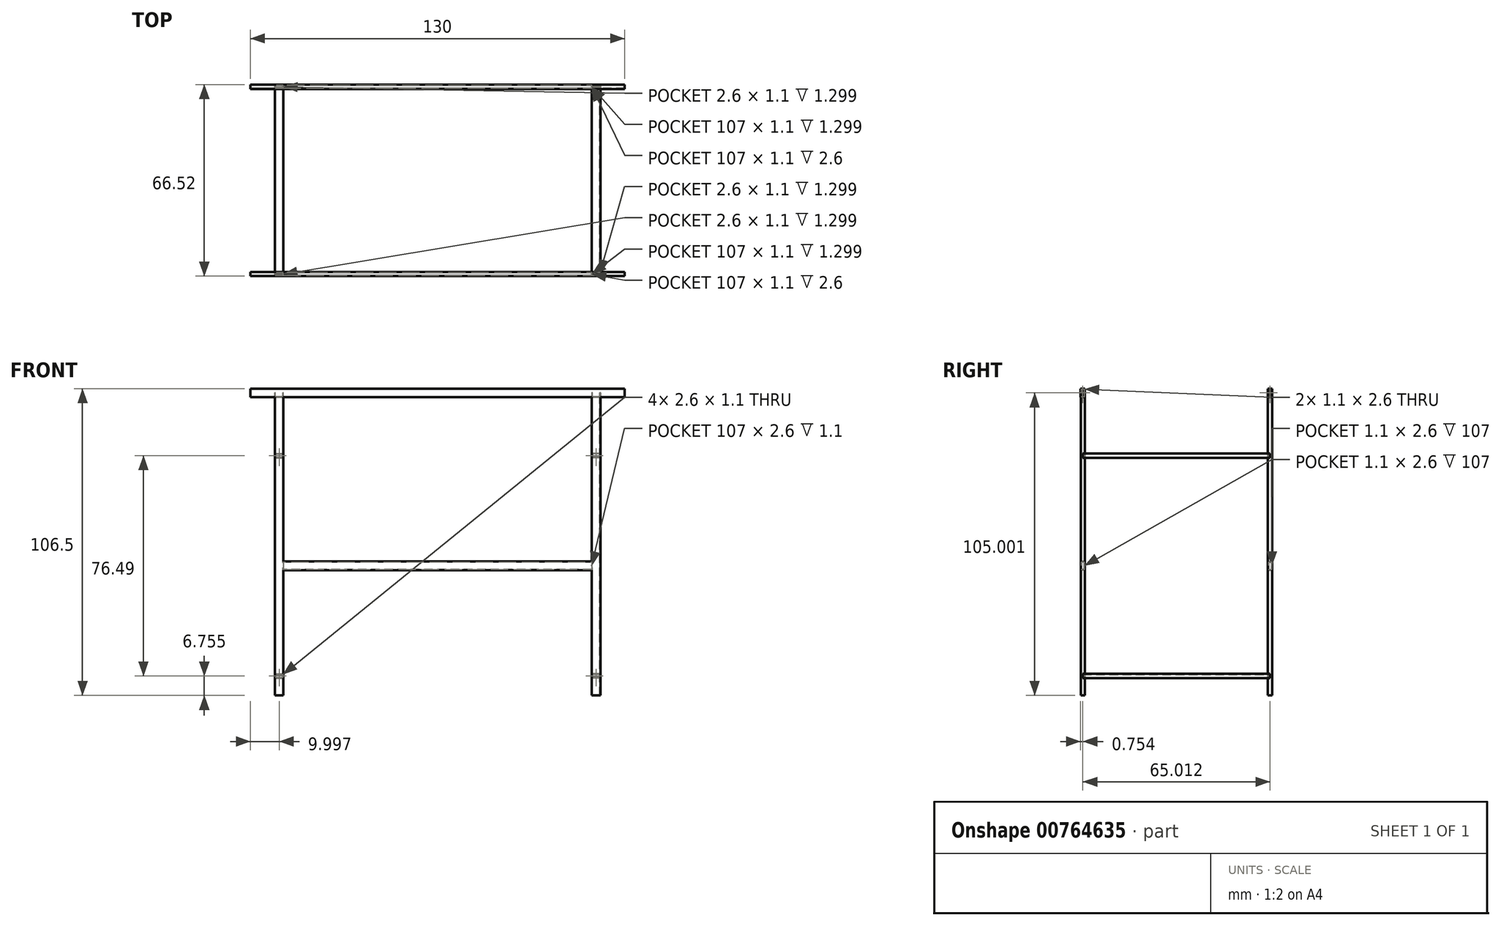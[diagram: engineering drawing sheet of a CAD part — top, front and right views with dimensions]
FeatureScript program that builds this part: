
annotation { "Feature Type Name" : "Feature", "Feature Type Description" : "" }
export const myFeature = defineFeature(function(context is Context, id is Id, definition is map)
    precondition{}
    {
        {
            var Q0;
            Q0=qCreatedBy(makeId("Top.planeOp"),FACE);
            cPlane(context, id + "F0", {"entities" : qUnion([Q0]), "cplaneType" : CPlaneType.OFFSET, "offset" : 60 * mm, "width" : 150 * mm, "height" : 150 * mm});
        }
        {
            var Q0;
            Q0=qCreatedBy(id+"F0.planeOp",FACE);
            var sketch = newSketch(context, id + "F1", { "sketchPlane" : qUnion([Q0])});
            skLineSegment(sketch, "E0", {"start": v(0, 0) * mm, "end": v(-65, 0) * mm, "construction": true});
            skLineSegment(sketch, "E1", {"start": v(-65, 0) * mm, "end": v(-65, 32.5) * mm, "construction": true});
            skSolve(sketch);
        }
        {
            var Q0;
            Q0=qCreatedBy(makeId("Right.planeOp"),FACE);
            cPlane(context, id + "F2", {"entities" : qUnion([Q0]), "cplaneType" : CPlaneType.OFFSET, "offset" : 65 * mm, "oppositeDirection" : true, "width" : 150 * mm, "height" : 150 * mm});
        }
        {
            var Q0;
            Q0=qCreatedBy(id+"F2.planeOp",FACE);
            var sketch = newSketch(context, id + "F3", { "sketchPlane" : qUnion([Q0])});
            skLineSegment(sketch, "E2.bottom", {"start": v(33.26, 61.5) * mm, "end": v(31.76, 61.5) * mm});
            skLineSegment(sketch, "E2.top", {"start": v(33.26, 58.5) * mm, "end": v(31.76, 58.5) * mm});
            skLineSegment(sketch, "E2.left", {"start": v(33.26, 61.5) * mm, "end": v(33.26, 58.5) * mm});
            skLineSegment(sketch, "E2.right", {"start": v(31.76, 61.5) * mm, "end": v(31.76, 58.5) * mm});
            skPoint(sketch, "E2.middle", {"position": v(32.5, 60) * mm});
            skLineSegment(sketch, "E3.bottom", {"start": v(33.06, 61.3) * mm, "end": v(31.96, 61.3) * mm});
            skLineSegment(sketch, "E3.top", {"start": v(33.06, 58.7) * mm, "end": v(31.96, 58.7) * mm});
            skLineSegment(sketch, "E3.left", {"start": v(33.06, 61.3) * mm, "end": v(33.06, 58.7) * mm});
            skLineSegment(sketch, "E3.right", {"start": v(31.96, 61.3) * mm, "end": v(31.96, 58.7) * mm});
            skSolve(sketch);
        }
        {
            var Q0;
            Q0=makeQuery(id+"F3.imprint","IMPRINT",FACE,{"disambiguationData":[TD([[makeQuery(id+"F3.imprint","IMPRINT",EDGE,{"derivedFrom":sQuery(id+"F3.wireOp",EDGE,"E2.bottom")}),1.0]])]});
            extrude(context, id + "F4", {"entities" : qUnion([Q0]), "depth" : 130 * mm, "offsetDistance" : 25 * mm});
        }
        {
            var Q0;
            Q0=makeQuery(id+"F4.opExtrude","SWEPT_BODY",BODY,{"disambiguationData":[OSD([sQuery(id+"F3.wireOp",EDGE,"E2.bottom"),sQuery(id+"F3.wireOp",EDGE,"E2.top"),sQuery(id+"F3.wireOp",EDGE,"E2.left"),sQuery(id+"F3.wireOp",EDGE,"E2.right"),sQuery(id+"F3.wireOp",EDGE,"E3.bottom"),sQuery(id+"F3.wireOp",EDGE,"E3.top"),sQuery(id+"F3.wireOp",EDGE,"E3.left"),sQuery(id+"F3.wireOp",EDGE,"E3.right")])]});
            var Q1;
            Q1=qCreatedBy(makeId("Front.planeOp"),FACE);
            mirror(context, id + "F5", {"entities" : qUnion([Q0]), "mirrorPlane" : qUnion([Q1])});
        }
        {
            var Q0;
            Q0=qCreatedBy(id+"F0.planeOp",FACE);
            var sketch = newSketch(context, id + "F6", { "sketchPlane" : qUnion([Q0])});
            skLineSegment(sketch, "E4", {"start": v(0, -49.29) * mm, "end": v(0, 13.23) * mm, "construction": true});
            skLineSegment(sketch, "E5", {"start": v(0, -32.5) * mm, "end": v(-55, -32.5) * mm, "construction": true});
            skLineSegment(sketch, "E6.bottom", {"start": v(-53.5, -33.25) * mm, "end": v(-56.5, -33.25) * mm});
            skLineSegment(sketch, "E6.top", {"start": v(-53.5, -31.75) * mm, "end": v(-56.5, -31.75) * mm});
            skLineSegment(sketch, "E6.left", {"start": v(-53.5, -33.25) * mm, "end": v(-53.5, -31.75) * mm});
            skLineSegment(sketch, "E6.right", {"start": v(-56.5, -33.25) * mm, "end": v(-56.5, -31.75) * mm});
            skPoint(sketch, "E6.middle", {"position": v(-55, -32.5) * mm});
            skLineSegment(sketch, "E7.bottom", {"start": v(-53.7, -33.05) * mm, "end": v(-56.3, -33.05) * mm});
            skLineSegment(sketch, "E7.top", {"start": v(-53.7, -31.95) * mm, "end": v(-56.3, -31.95) * mm});
            skLineSegment(sketch, "E7.left", {"start": v(-53.7, -33.05) * mm, "end": v(-53.7, -31.95) * mm});
            skLineSegment(sketch, "E7.right", {"start": v(-56.3, -33.05) * mm, "end": v(-56.3, -31.95) * mm});
            skSolve(sketch);
        }
        {
            var Q0;
            Q0=qSketchRegion(id+"F6",true);
            extrude(context, id + "F7", {"entities" : qUnion([Q0]), "oppositeDirection" : true, "depth" : 105 * mm, "offsetDistance" : 25 * mm});
        }
        {
            var Q0;
            Q0=makeQuery(id+"F7.opExtrude","SWEPT_BODY",BODY,{"disambiguationData":[OSD([sQuery(id+"F6.wireOp",EDGE,"E6.bottom"),sQuery(id+"F6.wireOp",EDGE,"E6.top"),sQuery(id+"F6.wireOp",EDGE,"E6.left"),sQuery(id+"F6.wireOp",EDGE,"E6.right"),sQuery(id+"F6.wireOp",EDGE,"E7.bottom"),sQuery(id+"F6.wireOp",EDGE,"E7.top"),sQuery(id+"F6.wireOp",EDGE,"E7.left"),sQuery(id+"F6.wireOp",EDGE,"E7.right")])]});
            var Q1;
            Q1=qCreatedBy(makeId("Right.planeOp"),FACE);
            mirror(context, id + "F8", {"operationType" : NewBodyOperationType.ADD, "entities" : qUnion([Q0]), "mirrorPlane" : qUnion([Q1])});
        }
        {
            var Q0;
            Q0=makeQuery(id+"F5.opPattern","COPY",BODY,{"derivedFrom":makeQuery(id+"F4.opExtrude","SWEPT_BODY",BODY,{"disambiguationData":[OSD([sQuery(id+"F3.wireOp",EDGE,"E2.bottom"),sQuery(id+"F3.wireOp",EDGE,"E2.top"),sQuery(id+"F3.wireOp",EDGE,"E2.left"),sQuery(id+"F3.wireOp",EDGE,"E2.right"),sQuery(id+"F3.wireOp",EDGE,"E3.bottom"),sQuery(id+"F3.wireOp",EDGE,"E3.top"),sQuery(id+"F3.wireOp",EDGE,"E3.left"),sQuery(id+"F3.wireOp",EDGE,"E3.right")])]}),"instanceName":"1"});
            var Q1;
            Q1=qCreatedBy(makeId("Front.planeOp"),FACE);
            mirror(context, id + "F9", {"operationType" : NewBodyOperationType.ADD, "entities" : qUnion([Q0]), "mirrorPlane" : qUnion([Q1])});
        }
        {
            var Q0;
            Q0=qCreatedBy(makeId("Front.planeOp"),FACE);
            var sketch = newSketch(context, id + "F10", { "sketchPlane" : qUnion([Q0])});
            skLineSegment(sketch, "E8", {"start": v(53.5, 56.46) * mm, "end": v(56.5, 56.46) * mm, "construction": true});
            skLineSegment(sketch, "E9", {"start": v(55, 58.24) * mm, "end": v(55, 38.24) * mm, "construction": true});
            skPoint(sketch, "E9.startSnap0", {"position": v(55, 56.46) * mm});
            skLineSegment(sketch, "E10.bottom", {"start": v(56.5, 39) * mm, "end": v(53.5, 39) * mm});
            skLineSegment(sketch, "E10.top", {"start": v(56.5, 37.5) * mm, "end": v(53.5, 37.5) * mm});
            skLineSegment(sketch, "E10.left", {"start": v(56.5, 39) * mm, "end": v(56.5, 37.5) * mm});
            skLineSegment(sketch, "E10.right", {"start": v(53.5, 39) * mm, "end": v(53.5, 37.5) * mm});
            skPoint(sketch, "E10.middle", {"position": v(55, 38.24) * mm});
            skLineSegment(sketch, "E11.bottom", {"start": v(56.3, 38.8) * mm, "end": v(53.7, 38.8) * mm});
            skLineSegment(sketch, "E11.top", {"start": v(56.3, 37.7) * mm, "end": v(53.7, 37.7) * mm});
            skLineSegment(sketch, "E11.left", {"start": v(56.3, 38.8) * mm, "end": v(56.3, 37.7) * mm});
            skLineSegment(sketch, "E11.right", {"start": v(53.7, 38.8) * mm, "end": v(53.7, 37.7) * mm});
            skSolve(sketch);
        }
        {
            var Q0;
            Q0=qSketchRegion(id+"F10",true);
            extrude(context, id + "F11", {"entities" : qUnion([Q0]), "endBound" : BoundingType.SYMMETRIC, "depth" : 65 * mm, "offsetDistance" : 25 * mm});
        }
        {
            var Q0;
            Q0=makeQuery(id+"F11.opExtrude","SWEPT_BODY",BODY,{"disambiguationData":[OSD([sQuery(id+"F10.wireOp",EDGE,"E10.bottom"),sQuery(id+"F10.wireOp",EDGE,"E10.top"),sQuery(id+"F10.wireOp",EDGE,"E10.left"),sQuery(id+"F10.wireOp",EDGE,"E10.right"),sQuery(id+"F10.wireOp",EDGE,"E11.bottom"),sQuery(id+"F10.wireOp",EDGE,"E11.top"),sQuery(id+"F10.wireOp",EDGE,"E11.left"),sQuery(id+"F10.wireOp",EDGE,"E11.right")])]});
            var Q1;
            Q1=qCreatedBy(makeId("Top.planeOp"),FACE);
            mirror(context, id + "F12", {"entities" : qUnion([Q0]), "mirrorPlane" : qUnion([Q1])});
        }
        {
            var Q0;
            Q0=makeQuery(id+"F11.opExtrude","SWEPT_BODY",BODY,{"disambiguationData":[OSD([sQuery(id+"F10.wireOp",EDGE,"E10.bottom"),sQuery(id+"F10.wireOp",EDGE,"E10.top"),sQuery(id+"F10.wireOp",EDGE,"E10.left"),sQuery(id+"F10.wireOp",EDGE,"E10.right"),sQuery(id+"F10.wireOp",EDGE,"E11.bottom"),sQuery(id+"F10.wireOp",EDGE,"E11.top"),sQuery(id+"F10.wireOp",EDGE,"E11.left"),sQuery(id+"F10.wireOp",EDGE,"E11.right")])]});
            var Q1;
            Q1=qCreatedBy(makeId("Right.planeOp"),FACE);
            mirror(context, id + "F13", {"entities" : qUnion([Q0]), "mirrorPlane" : qUnion([Q1])});
        }
        {
            var Q0;
            Q0=makeQuery(id+"F13.opPattern","COPY",BODY,{"derivedFrom":makeQuery(id+"F11.opExtrude","SWEPT_BODY",BODY,{"disambiguationData":[OSD([sQuery(id+"F10.wireOp",EDGE,"E10.bottom"),sQuery(id+"F10.wireOp",EDGE,"E10.top"),sQuery(id+"F10.wireOp",EDGE,"E10.left"),sQuery(id+"F10.wireOp",EDGE,"E10.right"),sQuery(id+"F10.wireOp",EDGE,"E11.bottom"),sQuery(id+"F10.wireOp",EDGE,"E11.top"),sQuery(id+"F10.wireOp",EDGE,"E11.left"),sQuery(id+"F10.wireOp",EDGE,"E11.right")])]}),"instanceName":"1"});
            var Q1;
            Q1=qCreatedBy(makeId("Top.planeOp"),FACE);
            mirror(context, id + "F14", {"entities" : qUnion([Q0]), "mirrorPlane" : qUnion([Q1])});
        }
        {
            var Q0;
            Q0=qCreatedBy(makeId("Right.planeOp"),FACE);
            var sketch = newSketch(context, id + "F15", { "sketchPlane" : qUnion([Q0])});
            skLineSegment(sketch, "E12", {"start": v(-33.25, 0) * mm, "end": v(-31.76, 0) * mm, "construction": true});
            skLineSegment(sketch, "E13.bottom", {"start": v(-31.76, 1.5) * mm, "end": v(-33.26, 1.5) * mm});
            skLineSegment(sketch, "E13.top", {"start": v(-31.76, -1.5) * mm, "end": v(-33.26, -1.5) * mm});
            skLineSegment(sketch, "E13.left", {"start": v(-31.76, 1.5) * mm, "end": v(-31.76, -1.5) * mm});
            skLineSegment(sketch, "E13.right", {"start": v(-33.26, 1.5) * mm, "end": v(-33.26, -1.5) * mm});
            skPoint(sketch, "E13.middle", {"position": v(-32.5, 0) * mm});
            skLineSegment(sketch, "E14.bottom", {"start": v(-31.96, 1.3) * mm, "end": v(-33.06, 1.3) * mm});
            skLineSegment(sketch, "E14.top", {"start": v(-31.96, -1.3) * mm, "end": v(-33.06, -1.3) * mm});
            skLineSegment(sketch, "E14.left", {"start": v(-31.96, 1.3) * mm, "end": v(-31.96, -1.3) * mm});
            skLineSegment(sketch, "E14.right", {"start": v(-33.06, 1.3) * mm, "end": v(-33.06, -1.3) * mm});
            skSolve(sketch);
        }
        {
            var Q0;
            Q0=qSketchRegion(id+"F15",true);
            extrude(context, id + "F16", {"entities" : qUnion([Q0]), "endBound" : BoundingType.SYMMETRIC, "depth" : 107 * mm, "offsetDistance" : 25 * mm});
        }
        {
            var Q0;
            Q0=makeQuery(id+"F16.opExtrude","SWEPT_BODY",BODY,{"disambiguationData":[OSD([sQuery(id+"F15.wireOp",EDGE,"E13.bottom"),sQuery(id+"F15.wireOp",EDGE,"E13.top"),sQuery(id+"F15.wireOp",EDGE,"E13.left"),sQuery(id+"F15.wireOp",EDGE,"E13.right"),sQuery(id+"F15.wireOp",EDGE,"E14.bottom"),sQuery(id+"F15.wireOp",EDGE,"E14.top"),sQuery(id+"F15.wireOp",EDGE,"E14.left"),sQuery(id+"F15.wireOp",EDGE,"E14.right")])]});
            var Q1;
            Q1=qCreatedBy(makeId("Front.planeOp"),FACE);
            mirror(context, id + "F17", {"operationType" : NewBodyOperationType.ADD, "entities" : qUnion([Q0]), "mirrorPlane" : qUnion([Q1])});
        }
    });
